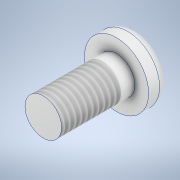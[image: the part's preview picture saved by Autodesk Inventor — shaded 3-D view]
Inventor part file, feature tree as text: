
AUTODESK INVENTOR PART (.ipt)
format: ipt  version: 2021 (Build 250183000, 183)  size: 146,944 bytes
history: native  units: in
note: dims shown in document units (in); Inventor stores cm internally (conversion verified against a paired STEP export)
features: other x2, thread x1
ambient origin geometry x8: Origin, YZ Plane, XZ Plane, XY Plane, X Axis, Y Axis, Z Axis, Center Point
bodies: Body1 (feature_tree)
feature tree (3):
  other  "Sólido2"
  thread  "Rosca1"  [1 undecoded]
  other  "Sólido1"
note: 1 required parameter value undecoded (feature->parameter linkage not recoverable at this tier; creation-order binding heuristic only, values carry confidence <= 0.55)
